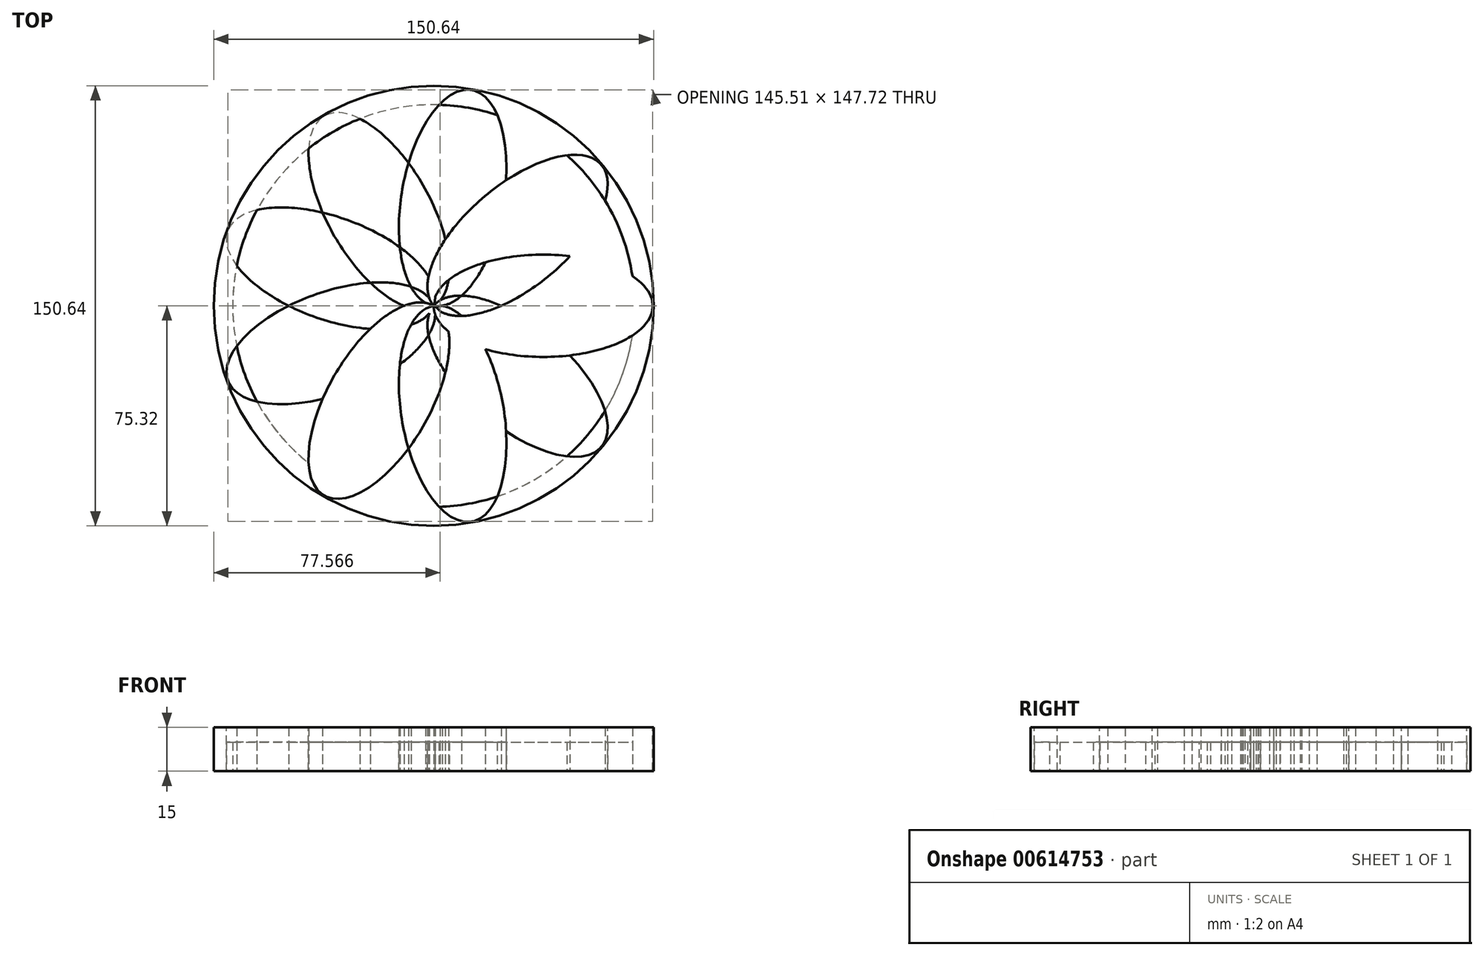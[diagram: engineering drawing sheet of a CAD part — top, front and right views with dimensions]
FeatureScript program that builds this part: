
annotation { "Feature Type Name" : "Feature", "Feature Type Description" : "" }
export const myFeature = defineFeature(function(context is Context, id is Id, definition is map)
    precondition{}
    {
        {
            var Q0;
            Q0=qCreatedBy(makeId("Top.planeOp"),FACE);
            var sketch = newSketch(context, id + "F0", { "sketchPlane" : qUnion([Q0])});
            skEllipse(sketch, "E0", {"center": v(37.5, 0) * mm, "majorRadius": 37.5 * mm, "minorRadius": 17.5 * mm, "majorAxis": v(-1, 0)});
            skEllipse(sketch, "E1.1.0", {"center": v(-18.75, -32.48) * mm, "majorRadius": 37.5 * mm, "minorRadius": 17.5 * mm, "majorAxis": v(0.5, 0.87)});
            skEllipse(sketch, "E1.2.0", {"center": v(-18.75, 32.48) * mm, "majorRadius": 37.5 * mm, "minorRadius": 17.5 * mm, "majorAxis": v(0.5, -0.87)});
            skPoint(sketch, "E1.center", {"position": v(0, 0) * mm});
            skLineSegment(sketch, "E1.anchor1", {"start": v(0, 0) * mm, "end": v(37.5, 0) * mm, "construction": true});
            skLineSegment(sketch, "E1.anchor2", {"start": v(0, 0) * mm, "end": v(-18.75, 32.48) * mm, "construction": true});
            skEllipse(sketch, "E2.1.0", {"center": v(-35.24, 12.83) * mm, "majorRadius": 37.5 * mm, "minorRadius": 17.5 * mm, "majorAxis": v(0.94, -0.34)});
            skEllipse(sketch, "E2.2.0", {"center": v(-35.24, -12.83) * mm, "majorRadius": 37.5 * mm, "minorRadius": 17.5 * mm, "majorAxis": v(0.94, 0.34)});
            skEllipse(sketch, "E2.3.0", {"center": v(-18.75, -32.48) * mm, "majorRadius": 37.5 * mm, "minorRadius": 17.5 * mm, "majorAxis": v(0.5, 0.87)});
            skEllipse(sketch, "E2.4.0", {"center": v(6.51, -36.93) * mm, "majorRadius": 37.5 * mm, "minorRadius": 17.5 * mm, "majorAxis": v(-0.17, 0.98)});
            skEllipse(sketch, "E2.5.0", {"center": v(28.73, -24.1) * mm, "majorRadius": 37.5 * mm, "minorRadius": 17.5 * mm, "majorAxis": v(-0.77, 0.64)});
            skEllipse(sketch, "E2.6.0", {"center": v(37.5, 0) * mm, "majorRadius": 37.5 * mm, "minorRadius": 17.5 * mm, "majorAxis": v(-1, 0)});
            skEllipse(sketch, "E2.7.0", {"center": v(28.73, 24.1) * mm, "majorRadius": 37.5 * mm, "minorRadius": 17.5 * mm, "majorAxis": v(-0.77, -0.64)});
            skEllipse(sketch, "E2.8.0", {"center": v(6.51, 36.93) * mm, "majorRadius": 37.5 * mm, "minorRadius": 17.5 * mm, "majorAxis": v(-0.17, -0.98)});
            skCircle(sketch, "E3", {"center": v(0, 0) * mm, "radius": 75.32 * mm});
            skCircle(sketch, "E4", {"center": v(0, 0) * mm, "radius": 68.82 * mm});
            skSolve(sketch);
        }
        {
            var Q0;
            {var subQ0=sQuery(id+"F0.wireOp",EDGE,"E2.3.0");var subQ1=sQuery(id+"F0.wireOp",EDGE,"E2.1.0");var subQ2=makeQuery(id+"F0.imprint","INTERSECT",VERTEX,{"derivedFrom":[subQ1,subQ0]});Q0=makeQuery(id+"F0.imprint","IMPRINT",FACE,{"disambiguationData":[TD([[makeQuery(id+"F0.imprint","IMPRINT",EDGE,{"disambiguationData":[TD([[subQ2,-1.0]])],"derivedFrom":subQ1}),-1.0]])]});}
            var Q1;
            {var subQ0=sQuery(id+"F0.wireOp",EDGE,"E2.2.0");var subQ1=sQuery(id+"F0.wireOp",EDGE,"E1.2.0");var subQ2=makeQuery(id+"F0.imprint","INTERSECT",VERTEX,{"derivedFrom":[subQ1,subQ0]});Q1=makeQuery(id+"F0.imprint","IMPRINT",FACE,{"disambiguationData":[TD([[makeQuery(id+"F0.imprint","IMPRINT",EDGE,{"disambiguationData":[TD([[subQ2,-1.0]])],"derivedFrom":subQ1}),-1.0]])]});}
            var Q2;
            {var subQ0=sQuery(id+"F0.wireOp",EDGE,"E2.1.0");var subQ1=sQuery(id+"F0.wireOp",EDGE,"E1.2.0");var subQ2=makeQuery(id+"F0.imprint","INTERSECT",VERTEX,{"derivedFrom":[subQ1,subQ0]});Q2=makeQuery(id+"F0.imprint","IMPRINT",FACE,{"disambiguationData":[TD([[makeQuery(id+"F0.imprint","IMPRINT",EDGE,{"disambiguationData":[TD([[subQ2,-1.0]])],"derivedFrom":subQ1}),1.0]])]});}
            var Q3;
            {var subQ0=sQuery(id+"F0.wireOp",EDGE,"E2.7.0");var subQ1=sQuery(id+"F0.wireOp",EDGE,"E1.2.0");var subQ2=makeQuery(id+"F0.imprint","INTERSECT",VERTEX,{"derivedFrom":[subQ1,subQ0]});Q3=makeQuery(id+"F0.imprint","IMPRINT",FACE,{"disambiguationData":[TD([[makeQuery(id+"F0.imprint","IMPRINT",EDGE,{"disambiguationData":[TD([[subQ2,-1.0]])],"derivedFrom":subQ1}),1.0]])]});}
            var Q4;
            {var subQ0=sQuery(id+"F0.wireOp",EDGE,"E2.6.0");var subQ1=sQuery(id+"F0.wireOp",EDGE,"E1.2.0");var subQ2=makeQuery(id+"F0.imprint","INTERSECT",VERTEX,{"derivedFrom":[subQ1,subQ0]});Q4=makeQuery(id+"F0.imprint","IMPRINT",FACE,{"disambiguationData":[TD([[makeQuery(id+"F0.imprint","IMPRINT",EDGE,{"disambiguationData":[TD([[subQ2,-1.0]])],"derivedFrom":subQ1}),-1.0]])]});}
            var Q5;
            {var subQ0=sQuery(id+"F0.wireOp",EDGE,"E2.7.0");var subQ1=sQuery(id+"F0.wireOp",EDGE,"E2.5.0");var subQ2=makeQuery(id+"F0.imprint","INTERSECT",VERTEX,{"derivedFrom":[subQ1,subQ0]});Q5=makeQuery(id+"F0.imprint","IMPRINT",FACE,{"disambiguationData":[TD([[makeQuery(id+"F0.imprint","IMPRINT",EDGE,{"disambiguationData":[TD([[subQ2,-1.0]])],"derivedFrom":subQ1}),-1.0]])]});}
            var Q6;
            {var subQ0=sQuery(id+"F0.wireOp",EDGE,"E2.6.0");var subQ1=sQuery(id+"F0.wireOp",EDGE,"E2.4.0");var subQ2=makeQuery(id+"F0.imprint","INTERSECT",VERTEX,{"derivedFrom":[subQ1,subQ0]});Q6=makeQuery(id+"F0.imprint","IMPRINT",FACE,{"disambiguationData":[TD([[makeQuery(id+"F0.imprint","IMPRINT",EDGE,{"disambiguationData":[TD([[subQ2,-1.0]])],"derivedFrom":subQ1}),-1.0]])]});}
            var Q7;
            {var subQ0=sQuery(id+"F0.wireOp",EDGE,"E2.5.0");var subQ1=sQuery(id+"F0.wireOp",EDGE,"E2.3.0");var subQ2=makeQuery(id+"F0.imprint","INTERSECT",VERTEX,{"derivedFrom":[subQ1,subQ0]});Q7=makeQuery(id+"F0.imprint","IMPRINT",FACE,{"disambiguationData":[TD([[makeQuery(id+"F0.imprint","IMPRINT",EDGE,{"disambiguationData":[TD([[subQ2,-1.0]])],"derivedFrom":subQ1}),-1.0]])]});}
            var Q8;
            {var subQ0=sQuery(id+"F0.wireOp",EDGE,"E2.4.0");var subQ1=sQuery(id+"F0.wireOp",EDGE,"E2.2.0");var subQ2=makeQuery(id+"F0.imprint","INTERSECT",VERTEX,{"derivedFrom":[subQ1,subQ0]});Q8=makeQuery(id+"F0.imprint","IMPRINT",FACE,{"disambiguationData":[TD([[makeQuery(id+"F0.imprint","IMPRINT",EDGE,{"disambiguationData":[TD([[subQ2,-1.0]])],"derivedFrom":subQ1}),-1.0]])]});}
            var Q9;
            {var subQ0=sQuery(id+"F0.wireOp",EDGE,"E2.7.0");var subQ1=sQuery(id+"F0.wireOp",EDGE,"E2.2.0");var subQ2=makeQuery(id+"F0.imprint","INTERSECT",VERTEX,{"derivedFrom":[subQ1,subQ0]});Q9=makeQuery(id+"F0.imprint","IMPRINT",FACE,{"disambiguationData":[TD([[makeQuery(id+"F0.imprint","IMPRINT",EDGE,{"disambiguationData":[TD([[subQ2,-1.0]])],"derivedFrom":subQ1}),1.0]])]});}
            var Q10;
            {var subQ0=sQuery(id+"F0.wireOp",EDGE,"E2.6.0");var subQ1=sQuery(id+"F0.wireOp",EDGE,"E2.1.0");var subQ2=makeQuery(id+"F0.imprint","INTERSECT",VERTEX,{"derivedFrom":[subQ1,subQ0]});Q10=makeQuery(id+"F0.imprint","IMPRINT",FACE,{"disambiguationData":[TD([[makeQuery(id+"F0.imprint","IMPRINT",EDGE,{"disambiguationData":[TD([[subQ2,-1.0]])],"derivedFrom":subQ1}),1.0]])]});}
            var Q11;
            {var subQ0=sQuery(id+"F0.wireOp",EDGE,"E2.5.0");var subQ1=sQuery(id+"F0.wireOp",EDGE,"E1.2.0");var subQ2=makeQuery(id+"F0.imprint","INTERSECT",VERTEX,{"derivedFrom":[subQ1,subQ0]});Q11=makeQuery(id+"F0.imprint","IMPRINT",FACE,{"disambiguationData":[TD([[makeQuery(id+"F0.imprint","IMPRINT",EDGE,{"disambiguationData":[TD([[subQ2,-1.0]])],"derivedFrom":subQ1}),1.0]])]});}
            var Q12;
            {var subQ0=sQuery(id+"F0.wireOp",EDGE,"E2.5.0");var subQ1=sQuery(id+"F0.wireOp",EDGE,"E1.2.0");var subQ2=makeQuery(id+"F0.imprint","INTERSECT",VERTEX,{"derivedFrom":[subQ1,subQ0]});Q12=makeQuery(id+"F0.imprint","IMPRINT",FACE,{"disambiguationData":[TD([[makeQuery(id+"F0.imprint","IMPRINT",EDGE,{"disambiguationData":[TD([[subQ2,1.0]])],"derivedFrom":subQ0}),1.0]])]});}
            var Q13;
            {var subQ0=sQuery(id+"F0.wireOp",EDGE,"E2.7.0");var subQ4=sQuery(id+"F0.wireOp",EDGE,"E2.4.0");var subQ6=makeQuery(id+"F0.imprint","INTERSECT",VERTEX,{"derivedFrom":[subQ4,subQ0]});Q13=makeQuery(id+"F0.imprint","IMPRINT",FACE,{"disambiguationData":[TD([[makeQuery(id+"F0.imprint","IMPRINT",EDGE,{"disambiguationData":[TD([[subQ6,-1.0]])],"derivedFrom":subQ4}),1.0]])]});}
            var Q14;
            {var subQ0=sQuery(id+"F0.wireOp",EDGE,"E2.6.0");var subQ4=sQuery(id+"F0.wireOp",EDGE,"E2.3.0");var subQ6=makeQuery(id+"F0.imprint","INTERSECT",VERTEX,{"derivedFrom":[subQ4,subQ0]});Q14=makeQuery(id+"F0.imprint","IMPRINT",FACE,{"disambiguationData":[TD([[makeQuery(id+"F0.imprint","IMPRINT",EDGE,{"disambiguationData":[TD([[subQ6,-1.0]])],"derivedFrom":subQ4}),1.0]])]});}
            var Q15;
            {var subQ0=sQuery(id+"F0.wireOp",EDGE,"E2.5.0");var subQ4=sQuery(id+"F0.wireOp",EDGE,"E2.2.0");var subQ6=makeQuery(id+"F0.imprint","INTERSECT",VERTEX,{"derivedFrom":[subQ4,subQ0]});Q15=makeQuery(id+"F0.imprint","IMPRINT",FACE,{"disambiguationData":[TD([[makeQuery(id+"F0.imprint","IMPRINT",EDGE,{"disambiguationData":[TD([[subQ6,-1.0]])],"derivedFrom":subQ4}),1.0]])]});}
            var Q16;
            {var subQ0=sQuery(id+"F0.wireOp",EDGE,"E2.4.0");var subQ4=sQuery(id+"F0.wireOp",EDGE,"E2.1.0");var subQ6=makeQuery(id+"F0.imprint","INTERSECT",VERTEX,{"derivedFrom":[subQ4,subQ0]});Q16=makeQuery(id+"F0.imprint","IMPRINT",FACE,{"disambiguationData":[TD([[makeQuery(id+"F0.imprint","IMPRINT",EDGE,{"disambiguationData":[TD([[subQ6,-1.0]])],"derivedFrom":subQ4}),1.0]])]});}
            var Q17;
            {var subQ0=sQuery(id+"F0.wireOp",EDGE,"E2.3.0");var subQ1=sQuery(id+"F0.wireOp",EDGE,"E1.2.0");var subQ2=makeQuery(id+"F0.imprint","INTERSECT",VERTEX,{"derivedFrom":[subQ1,subQ0]});Q17=makeQuery(id+"F0.imprint","IMPRINT",FACE,{"disambiguationData":[TD([[makeQuery(id+"F0.imprint","IMPRINT",EDGE,{"disambiguationData":[TD([[subQ2,-1.0]])],"derivedFrom":subQ1}),1.0]])]});}
            var Q18;
            Q18=makeQuery(id+"F0.imprint","IMPRINT",FACE,{"disambiguationData":[TD([[makeQuery(id+"F0.imprint","IMPRINT",EDGE,{"derivedFrom":sQuery(id+"F0.wireOp",EDGE,"E3")}),1.0]])]});
            var Q19;
            {var subQ0=sQuery(id+"F0.wireOp",EDGE,"E4");var subQ1=sQuery(id+"F0.wireOp",EDGE,"E1.2.0");var subQ2=makeQuery(id+"F0.imprint","INTERSECT",VERTEX,{"disambiguationData":[OD(1.0)],"derivedFrom":[subQ1,subQ0]});Q19=makeQuery(id+"F0.imprint","IMPRINT",FACE,{"disambiguationData":[TD([[makeQuery(id+"F0.imprint","IMPRINT",EDGE,{"disambiguationData":[TD([[subQ2,-1.0]])],"derivedFrom":subQ1}),-1.0]])]});}
            var Q20;
            {var subQ0=sQuery(id+"F0.wireOp",EDGE,"E2.8.0");var subQ1=sQuery(id+"F0.wireOp",EDGE,"E1.2.0");var subQ2=makeQuery(id+"F0.imprint","INTERSECT",VERTEX,{"derivedFrom":[subQ1,subQ0]});Q20=makeQuery(id+"F0.imprint","IMPRINT",FACE,{"disambiguationData":[TD([[makeQuery(id+"F0.imprint","IMPRINT",EDGE,{"disambiguationData":[TD([[subQ2,-1.0]])],"derivedFrom":subQ1}),-1.0]])]});}
            var Q21;
            {var subQ0=sQuery(id+"F0.wireOp",EDGE,"E4");var subQ1=sQuery(id+"F0.wireOp",EDGE,"E2.7.0");var subQ2=makeQuery(id+"F0.imprint","INTERSECT",VERTEX,{"disambiguationData":[OD(1.0)],"derivedFrom":[subQ1,subQ0]});Q21=makeQuery(id+"F0.imprint","IMPRINT",FACE,{"disambiguationData":[TD([[makeQuery(id+"F0.imprint","IMPRINT",EDGE,{"disambiguationData":[TD([[subQ2,-1.0]])],"derivedFrom":subQ1}),-1.0]])]});}
            var Q22;
            {var subQ0=sQuery(id+"F0.wireOp",EDGE,"E4");var subQ1=sQuery(id+"F0.wireOp",EDGE,"E2.6.0");var subQ2=makeQuery(id+"F0.imprint","INTERSECT",VERTEX,{"disambiguationData":[OD(1.0)],"derivedFrom":[subQ1,subQ0]});Q22=makeQuery(id+"F0.imprint","IMPRINT",FACE,{"disambiguationData":[TD([[makeQuery(id+"F0.imprint","IMPRINT",EDGE,{"disambiguationData":[TD([[subQ2,-1.0]])],"derivedFrom":subQ1}),-1.0]])]});}
            var Q23;
            {var subQ0=sQuery(id+"F0.wireOp",EDGE,"E4");var subQ1=sQuery(id+"F0.wireOp",EDGE,"E2.5.0");var subQ2=makeQuery(id+"F0.imprint","INTERSECT",VERTEX,{"disambiguationData":[OD(1.0)],"derivedFrom":[subQ1,subQ0]});Q23=makeQuery(id+"F0.imprint","IMPRINT",FACE,{"disambiguationData":[TD([[makeQuery(id+"F0.imprint","IMPRINT",EDGE,{"disambiguationData":[TD([[subQ2,-1.0]])],"derivedFrom":subQ1}),-1.0]])]});}
            var Q24;
            {var subQ0=sQuery(id+"F0.wireOp",EDGE,"E4");var subQ1=sQuery(id+"F0.wireOp",EDGE,"E2.4.0");var subQ2=makeQuery(id+"F0.imprint","INTERSECT",VERTEX,{"disambiguationData":[OD(1.0)],"derivedFrom":[subQ1,subQ0]});Q24=makeQuery(id+"F0.imprint","IMPRINT",FACE,{"disambiguationData":[TD([[makeQuery(id+"F0.imprint","IMPRINT",EDGE,{"disambiguationData":[TD([[subQ2,-1.0]])],"derivedFrom":subQ1}),-1.0]])]});}
            var Q25;
            {var subQ0=sQuery(id+"F0.wireOp",EDGE,"E4");var subQ1=sQuery(id+"F0.wireOp",EDGE,"E2.3.0");var subQ2=makeQuery(id+"F0.imprint","INTERSECT",VERTEX,{"disambiguationData":[OD(1.0)],"derivedFrom":[subQ1,subQ0]});Q25=makeQuery(id+"F0.imprint","IMPRINT",FACE,{"disambiguationData":[TD([[makeQuery(id+"F0.imprint","IMPRINT",EDGE,{"disambiguationData":[TD([[subQ2,-1.0]])],"derivedFrom":subQ1}),-1.0]])]});}
            var Q26;
            {var subQ0=sQuery(id+"F0.wireOp",EDGE,"E4");var subQ1=sQuery(id+"F0.wireOp",EDGE,"E2.2.0");var subQ2=makeQuery(id+"F0.imprint","INTERSECT",VERTEX,{"disambiguationData":[OD(1.0)],"derivedFrom":[subQ1,subQ0]});Q26=makeQuery(id+"F0.imprint","IMPRINT",FACE,{"disambiguationData":[TD([[makeQuery(id+"F0.imprint","IMPRINT",EDGE,{"disambiguationData":[TD([[subQ2,-1.0]])],"derivedFrom":subQ1}),-1.0]])]});}
            var Q27;
            {var subQ0=sQuery(id+"F0.wireOp",EDGE,"E4");var subQ1=sQuery(id+"F0.wireOp",EDGE,"E2.1.0");var subQ2=makeQuery(id+"F0.imprint","INTERSECT",VERTEX,{"disambiguationData":[OD(1.0)],"derivedFrom":[subQ1,subQ0]});Q27=makeQuery(id+"F0.imprint","IMPRINT",FACE,{"disambiguationData":[TD([[makeQuery(id+"F0.imprint","IMPRINT",EDGE,{"disambiguationData":[TD([[subQ2,-1.0]])],"derivedFrom":subQ1}),-1.0]])]});}
            extrude(context, id + "F1", {"entities" : qUnion([Q0, Q1, Q2, Q3, Q4, Q5, Q6, Q7, Q8, Q9, Q10, Q11, Q12, Q13, Q14, Q15, Q16, Q17, Q18, Q19, Q20, Q21, Q22, Q23, Q24, Q25, Q26, Q27]), "depth" : 15 * mm, "offsetDistance" : 25 * mm});
        }
        {
            var Q0;
            {var subQ1=sQuery(id+"F0.wireOp",EDGE,"E2.1.0");var subQ3=sQuery(id+"F0.wireOp",EDGE,"E2.2.0");var subQ5=makeQuery(id+"F0.imprint","INTERSECT",VERTEX,{"derivedFrom":[subQ1,subQ3]});Q0=makeQuery(id+"F0.imprint","IMPRINT",FACE,{"disambiguationData":[TD([[makeQuery(id+"F0.imprint","IMPRINT",EDGE,{"disambiguationData":[TD([[subQ5,-1.0]])],"derivedFrom":subQ1}),-1.0]])]});}
            var Q1;
            {var subQ1=sQuery(id+"F0.wireOp",EDGE,"E1.2.0");var subQ3=sQuery(id+"F0.wireOp",EDGE,"E2.1.0");var subQ5=makeQuery(id+"F0.imprint","INTERSECT",VERTEX,{"derivedFrom":[subQ1,subQ3]});Q1=makeQuery(id+"F0.imprint","IMPRINT",FACE,{"disambiguationData":[TD([[makeQuery(id+"F0.imprint","IMPRINT",EDGE,{"disambiguationData":[TD([[subQ5,-1.0]])],"derivedFrom":subQ1}),-1.0]])]});}
            var Q2;
            {var subQ0=sQuery(id+"F0.wireOp",EDGE,"E2.8.0");var subQ1=sQuery(id+"F0.wireOp",EDGE,"E1.2.0");var subQ2=makeQuery(id+"F0.imprint","INTERSECT",VERTEX,{"derivedFrom":[subQ1,subQ0]});Q2=makeQuery(id+"F0.imprint","IMPRINT",FACE,{"disambiguationData":[TD([[makeQuery(id+"F0.imprint","IMPRINT",EDGE,{"disambiguationData":[TD([[subQ2,-1.0]])],"derivedFrom":subQ1}),1.0]])]});}
            var Q3;
            {var subQ1=sQuery(id+"F0.wireOp",EDGE,"E2.7.0");var subQ6=sQuery(id+"F0.wireOp",EDGE,"E1.2.0");var subQ8=makeQuery(id+"F0.imprint","INTERSECT",VERTEX,{"derivedFrom":[subQ6,subQ1]});Q3=makeQuery(id+"F0.imprint","IMPRINT",FACE,{"disambiguationData":[TD([[makeQuery(id+"F0.imprint","IMPRINT",EDGE,{"disambiguationData":[TD([[subQ8,-1.0]])],"derivedFrom":subQ6}),-1.0]])]});}
            var Q4;
            {var subQ1=sQuery(id+"F0.wireOp",EDGE,"E2.6.0");var subQ3=sQuery(id+"F0.wireOp",EDGE,"E2.7.0");var subQ5=makeQuery(id+"F0.imprint","INTERSECT",VERTEX,{"derivedFrom":[subQ1,subQ3]});Q4=makeQuery(id+"F0.imprint","IMPRINT",FACE,{"disambiguationData":[TD([[makeQuery(id+"F0.imprint","IMPRINT",EDGE,{"disambiguationData":[TD([[subQ5,-1.0]])],"derivedFrom":subQ1}),-1.0]])]});}
            var Q5;
            {var subQ1=sQuery(id+"F0.wireOp",EDGE,"E2.5.0");var subQ3=sQuery(id+"F0.wireOp",EDGE,"E2.6.0");var subQ5=makeQuery(id+"F0.imprint","INTERSECT",VERTEX,{"derivedFrom":[subQ1,subQ3]});Q5=makeQuery(id+"F0.imprint","IMPRINT",FACE,{"disambiguationData":[TD([[makeQuery(id+"F0.imprint","IMPRINT",EDGE,{"disambiguationData":[TD([[subQ5,-1.0]])],"derivedFrom":subQ1}),-1.0]])]});}
            var Q6;
            {var subQ1=sQuery(id+"F0.wireOp",EDGE,"E2.4.0");var subQ3=sQuery(id+"F0.wireOp",EDGE,"E2.5.0");var subQ5=makeQuery(id+"F0.imprint","INTERSECT",VERTEX,{"derivedFrom":[subQ1,subQ3]});Q6=makeQuery(id+"F0.imprint","IMPRINT",FACE,{"disambiguationData":[TD([[makeQuery(id+"F0.imprint","IMPRINT",EDGE,{"disambiguationData":[TD([[subQ5,-1.0]])],"derivedFrom":subQ1}),-1.0]])]});}
            var Q7;
            {var subQ1=sQuery(id+"F0.wireOp",EDGE,"E2.3.0");var subQ3=sQuery(id+"F0.wireOp",EDGE,"E2.4.0");var subQ8=makeQuery(id+"F0.imprint","INTERSECT",VERTEX,{"derivedFrom":[subQ1,subQ3]});Q7=makeQuery(id+"F0.imprint","IMPRINT",FACE,{"disambiguationData":[TD([[makeQuery(id+"F0.imprint","IMPRINT",EDGE,{"disambiguationData":[TD([[subQ8,-1.0]])],"derivedFrom":subQ1}),-1.0]])]});}
            var Q8;
            {var subQ1=sQuery(id+"F0.wireOp",EDGE,"E2.2.0");var subQ3=sQuery(id+"F0.wireOp",EDGE,"E2.3.0");var subQ5=makeQuery(id+"F0.imprint","INTERSECT",VERTEX,{"derivedFrom":[subQ1,subQ3]});Q8=makeQuery(id+"F0.imprint","IMPRINT",FACE,{"disambiguationData":[TD([[makeQuery(id+"F0.imprint","IMPRINT",EDGE,{"disambiguationData":[TD([[subQ5,-1.0]])],"derivedFrom":subQ1}),-1.0]])]});}
            extrude(context, id + "F2", {"entities" : qUnion([Q0, Q1, Q2, Q3, Q4, Q5, Q6, Q7, Q8]), "depth" : 10 * mm, "offsetDistance" : 25 * mm});
        }
        {
            var Q0;
            {var subQ0=sQuery(id+"F0.wireOp",EDGE,"E4");var subQ1=sQuery(id+"F0.wireOp",EDGE,"E2.4.0");var subQ2=makeQuery(id+"F0.imprint","INTERSECT",VERTEX,{"disambiguationData":[OD(0.0)],"derivedFrom":[subQ1,subQ0]});Q0=makeQuery(id+"F0.imprint","IMPRINT",FACE,{"disambiguationData":[TD([[makeQuery(id+"F0.imprint","IMPRINT",EDGE,{"disambiguationData":[TD([[subQ2,-1.0]])],"derivedFrom":subQ1}),1.0]])]});}
            var Q1;
            {var subQ0=sQuery(id+"F0.wireOp",EDGE,"E4");var subQ1=sQuery(id+"F0.wireOp",EDGE,"E2.5.0");var subQ2=makeQuery(id+"F0.imprint","INTERSECT",VERTEX,{"disambiguationData":[OD(0.0)],"derivedFrom":[subQ1,subQ0]});Q1=makeQuery(id+"F0.imprint","IMPRINT",FACE,{"disambiguationData":[TD([[makeQuery(id+"F0.imprint","IMPRINT",EDGE,{"disambiguationData":[TD([[subQ2,-1.0]])],"derivedFrom":subQ1}),1.0]])]});}
            var Q2;
            {var subQ0=sQuery(id+"F0.wireOp",EDGE,"E4");var subQ1=sQuery(id+"F0.wireOp",EDGE,"E2.6.0");var subQ2=makeQuery(id+"F0.imprint","INTERSECT",VERTEX,{"disambiguationData":[OD(0.0)],"derivedFrom":[subQ1,subQ0]});Q2=makeQuery(id+"F0.imprint","IMPRINT",FACE,{"disambiguationData":[TD([[makeQuery(id+"F0.imprint","IMPRINT",EDGE,{"disambiguationData":[TD([[subQ2,-1.0]])],"derivedFrom":subQ1}),1.0]])]});}
            var Q3;
            {var subQ0=sQuery(id+"F0.wireOp",EDGE,"E4");var subQ1=sQuery(id+"F0.wireOp",EDGE,"E2.7.0");var subQ2=makeQuery(id+"F0.imprint","INTERSECT",VERTEX,{"disambiguationData":[OD(0.0)],"derivedFrom":[subQ1,subQ0]});Q3=makeQuery(id+"F0.imprint","IMPRINT",FACE,{"disambiguationData":[TD([[makeQuery(id+"F0.imprint","IMPRINT",EDGE,{"disambiguationData":[TD([[subQ2,-1.0]])],"derivedFrom":subQ1}),1.0]])]});}
            var Q4;
            {var subQ0=sQuery(id+"F0.wireOp",EDGE,"E4");var subQ1=sQuery(id+"F0.wireOp",EDGE,"E2.8.0");var subQ2=makeQuery(id+"F0.imprint","INTERSECT",VERTEX,{"disambiguationData":[OD(0.0)],"derivedFrom":[subQ1,subQ0]});Q4=makeQuery(id+"F0.imprint","IMPRINT",FACE,{"disambiguationData":[TD([[makeQuery(id+"F0.imprint","IMPRINT",EDGE,{"disambiguationData":[TD([[subQ2,-1.0]])],"derivedFrom":subQ1}),1.0]])]});}
            var Q5;
            {var subQ0=sQuery(id+"F0.wireOp",EDGE,"E4");var subQ1=sQuery(id+"F0.wireOp",EDGE,"E1.2.0");var subQ2=makeQuery(id+"F0.imprint","INTERSECT",VERTEX,{"disambiguationData":[OD(0.0)],"derivedFrom":[subQ1,subQ0]});Q5=makeQuery(id+"F0.imprint","IMPRINT",FACE,{"disambiguationData":[TD([[makeQuery(id+"F0.imprint","IMPRINT",EDGE,{"disambiguationData":[TD([[subQ2,-1.0]])],"derivedFrom":subQ1}),1.0]])]});}
            var Q6;
            {var subQ0=sQuery(id+"F0.wireOp",EDGE,"E4");var subQ1=sQuery(id+"F0.wireOp",EDGE,"E2.1.0");var subQ2=makeQuery(id+"F0.imprint","INTERSECT",VERTEX,{"disambiguationData":[OD(0.0)],"derivedFrom":[subQ1,subQ0]});Q6=makeQuery(id+"F0.imprint","IMPRINT",FACE,{"disambiguationData":[TD([[makeQuery(id+"F0.imprint","IMPRINT",EDGE,{"disambiguationData":[TD([[subQ2,-1.0]])],"derivedFrom":subQ1}),1.0]])]});}
            var Q7;
            {var subQ0=sQuery(id+"F0.wireOp",EDGE,"E4");var subQ1=sQuery(id+"F0.wireOp",EDGE,"E2.2.0");var subQ2=makeQuery(id+"F0.imprint","INTERSECT",VERTEX,{"disambiguationData":[OD(0.0)],"derivedFrom":[subQ1,subQ0]});Q7=makeQuery(id+"F0.imprint","IMPRINT",FACE,{"disambiguationData":[TD([[makeQuery(id+"F0.imprint","IMPRINT",EDGE,{"disambiguationData":[TD([[subQ2,-1.0]])],"derivedFrom":subQ1}),1.0]])]});}
            var Q8;
            {var subQ0=sQuery(id+"F0.wireOp",EDGE,"E4");var subQ1=sQuery(id+"F0.wireOp",EDGE,"E2.3.0");var subQ2=makeQuery(id+"F0.imprint","INTERSECT",VERTEX,{"disambiguationData":[OD(0.0)],"derivedFrom":[subQ1,subQ0]});Q8=makeQuery(id+"F0.imprint","IMPRINT",FACE,{"disambiguationData":[TD([[makeQuery(id+"F0.imprint","IMPRINT",EDGE,{"disambiguationData":[TD([[subQ2,-1.0]])],"derivedFrom":subQ1}),1.0]])]});}
            extrude(context, id + "F3", {"entities" : qUnion([Q0, Q1, Q2, Q3, Q4, Q5, Q6, Q7, Q8]), "depth" : 10 * mm, "offsetDistance" : 25 * mm});
        }
        {
            var Q0;
            {var subQ0=sQuery(id+"F0.wireOp",EDGE,"E2.7.0");var subQ1=sQuery(id+"F0.wireOp",EDGE,"E2.1.0");var subQ2=makeQuery(id+"F0.imprint","INTERSECT",VERTEX,{"derivedFrom":[subQ1,subQ0]});Q0=makeQuery(id+"F0.imprint","IMPRINT",FACE,{"disambiguationData":[TD([[makeQuery(id+"F0.imprint","IMPRINT",EDGE,{"disambiguationData":[TD([[subQ2,-1.0]])],"derivedFrom":subQ1}),1.0]])]});}
            var Q1;
            {var subQ0=sQuery(id+"F0.wireOp",EDGE,"E2.6.0");var subQ1=sQuery(id+"F0.wireOp",EDGE,"E1.2.0");var subQ2=makeQuery(id+"F0.imprint","INTERSECT",VERTEX,{"derivedFrom":[subQ1,subQ0]});Q1=makeQuery(id+"F0.imprint","IMPRINT",FACE,{"disambiguationData":[TD([[makeQuery(id+"F0.imprint","IMPRINT",EDGE,{"disambiguationData":[TD([[subQ2,-1.0]])],"derivedFrom":subQ1}),1.0]])]});}
            var Q2;
            {var subQ0=sQuery(id+"F0.wireOp",EDGE,"E2.5.0");var subQ1=sQuery(id+"F0.wireOp",EDGE,"E1.2.0");var subQ2=makeQuery(id+"F0.imprint","INTERSECT",VERTEX,{"derivedFrom":[subQ1,subQ0]});Q2=makeQuery(id+"F0.imprint","IMPRINT",FACE,{"disambiguationData":[TD([[makeQuery(id+"F0.imprint","IMPRINT",EDGE,{"disambiguationData":[TD([[subQ2,-1.0]])],"derivedFrom":subQ1}),-1.0]])]});}
            var Q3;
            {var subQ0=sQuery(id+"F0.wireOp",EDGE,"E2.7.0");var subQ1=sQuery(id+"F0.wireOp",EDGE,"E2.4.0");var subQ2=makeQuery(id+"F0.imprint","INTERSECT",VERTEX,{"derivedFrom":[subQ1,subQ0]});Q3=makeQuery(id+"F0.imprint","IMPRINT",FACE,{"disambiguationData":[TD([[makeQuery(id+"F0.imprint","IMPRINT",EDGE,{"disambiguationData":[TD([[subQ2,-1.0]])],"derivedFrom":subQ1}),-1.0]])]});}
            var Q4;
            {var subQ0=sQuery(id+"F0.wireOp",EDGE,"E2.6.0");var subQ1=sQuery(id+"F0.wireOp",EDGE,"E2.3.0");var subQ2=makeQuery(id+"F0.imprint","INTERSECT",VERTEX,{"derivedFrom":[subQ1,subQ0]});Q4=makeQuery(id+"F0.imprint","IMPRINT",FACE,{"disambiguationData":[TD([[makeQuery(id+"F0.imprint","IMPRINT",EDGE,{"disambiguationData":[TD([[subQ2,-1.0]])],"derivedFrom":subQ1}),-1.0]])]});}
            var Q5;
            {var subQ0=sQuery(id+"F0.wireOp",EDGE,"E2.5.0");var subQ1=sQuery(id+"F0.wireOp",EDGE,"E2.2.0");var subQ2=makeQuery(id+"F0.imprint","INTERSECT",VERTEX,{"derivedFrom":[subQ1,subQ0]});Q5=makeQuery(id+"F0.imprint","IMPRINT",FACE,{"disambiguationData":[TD([[makeQuery(id+"F0.imprint","IMPRINT",EDGE,{"disambiguationData":[TD([[subQ2,-1.0]])],"derivedFrom":subQ1}),-1.0]])]});}
            var Q6;
            {var subQ0=sQuery(id+"F0.wireOp",EDGE,"E2.4.0");var subQ1=sQuery(id+"F0.wireOp",EDGE,"E2.1.0");var subQ2=makeQuery(id+"F0.imprint","INTERSECT",VERTEX,{"derivedFrom":[subQ1,subQ0]});Q6=makeQuery(id+"F0.imprint","IMPRINT",FACE,{"disambiguationData":[TD([[makeQuery(id+"F0.imprint","IMPRINT",EDGE,{"disambiguationData":[TD([[subQ2,-1.0]])],"derivedFrom":subQ1}),-1.0]])]});}
            var Q7;
            {var subQ0=sQuery(id+"F0.wireOp",EDGE,"E2.3.0");var subQ1=sQuery(id+"F0.wireOp",EDGE,"E1.2.0");var subQ2=makeQuery(id+"F0.imprint","INTERSECT",VERTEX,{"derivedFrom":[subQ1,subQ0]});Q7=makeQuery(id+"F0.imprint","IMPRINT",FACE,{"disambiguationData":[TD([[makeQuery(id+"F0.imprint","IMPRINT",EDGE,{"disambiguationData":[TD([[subQ2,-1.0]])],"derivedFrom":subQ1}),-1.0]])]});}
            var Q8;
            {var subQ0=sQuery(id+"F0.wireOp",EDGE,"E2.2.0");var subQ1=sQuery(id+"F0.wireOp",EDGE,"E1.2.0");var subQ2=makeQuery(id+"F0.imprint","INTERSECT",VERTEX,{"derivedFrom":[subQ1,subQ0]});Q8=makeQuery(id+"F0.imprint","IMPRINT",FACE,{"disambiguationData":[TD([[makeQuery(id+"F0.imprint","IMPRINT",EDGE,{"disambiguationData":[TD([[subQ2,-1.0]])],"derivedFrom":subQ1}),1.0]])]});}
            extrude(context, id + "F4", {"entities" : qUnion([Q0, Q1, Q2, Q3, Q4, Q5, Q6, Q7, Q8]), "depth" : 10 * mm, "offsetDistance" : 25 * mm});
        }
    });
